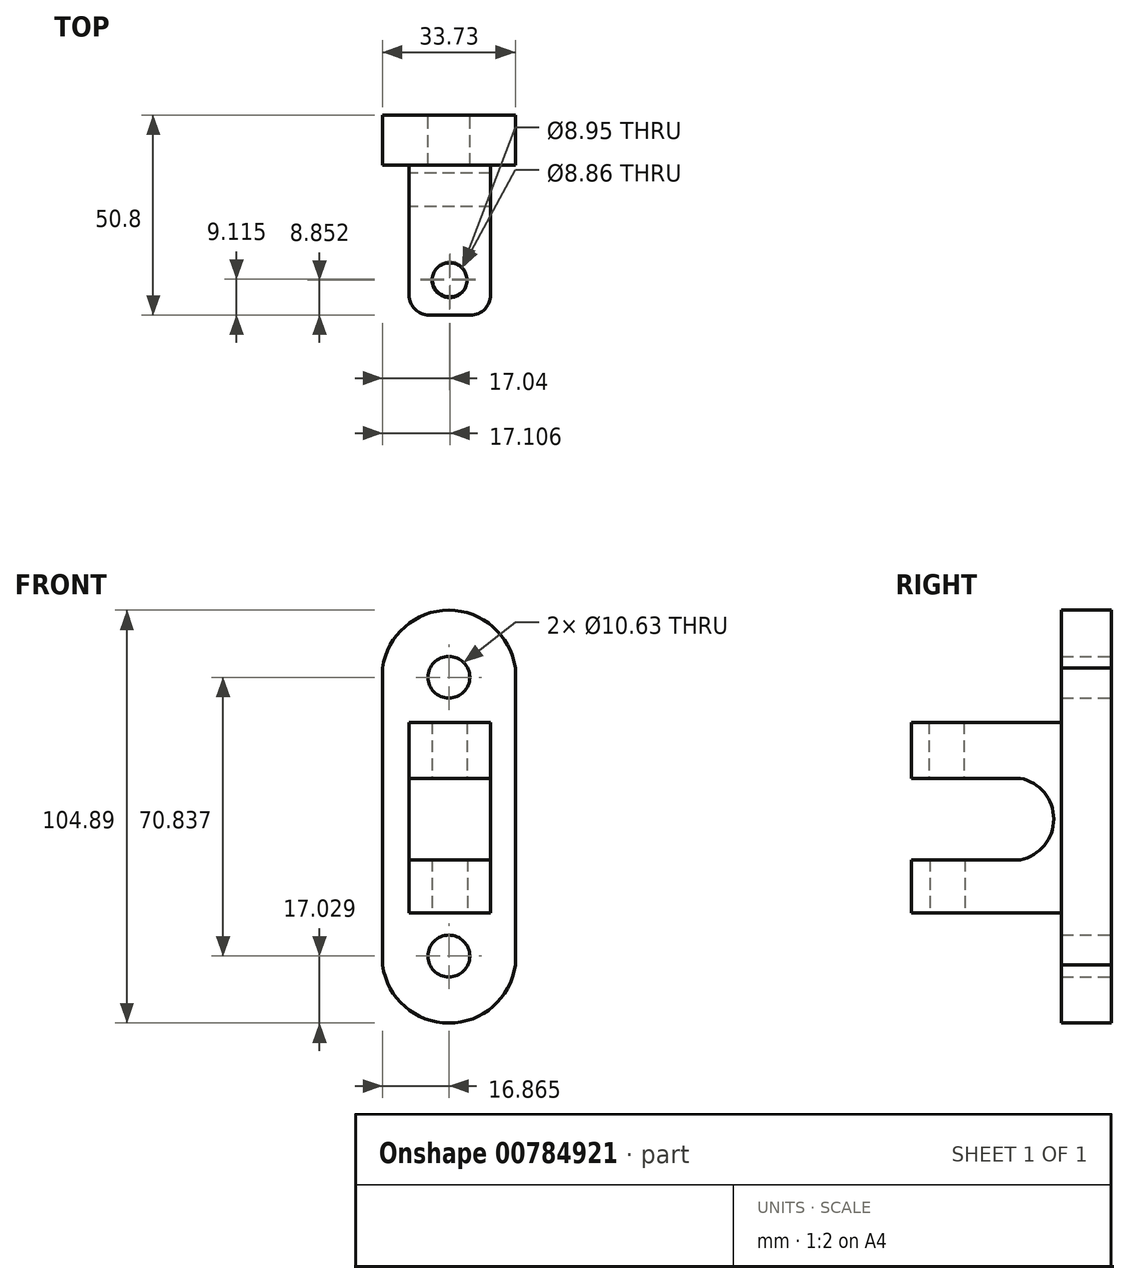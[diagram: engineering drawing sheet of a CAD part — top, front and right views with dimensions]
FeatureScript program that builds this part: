
annotation { "Feature Type Name" : "Feature", "Feature Type Description" : "" }
export const myFeature = defineFeature(function(context is Context, id is Id, definition is map)
    precondition{}
    {
        {
            var Q0;
            Q0=qCreatedBy(makeId("Front.planeOp"),FACE);
            var sketch = newSketch(context, id + "F0", { "sketchPlane" : qUnion([Q0])});
            skLineSegment(sketch, "E0", {"start": v(-23.01, 39.4) * mm, "end": v(-23.01, -36.03) * mm});
            skLineSegment(sketch, "E1", {"start": v(10.72, 39.4) * mm, "end": v(10.72, -36.03) * mm});
            skArc(sketch, "E2", {"start": v(10.72, 39.4) * mm, "mid": v(-6.15, 54.13) * mm, "end": v(-23.01, 39.4) * mm});
            skArc(sketch, "E3", {"start": v(-23.01, -36.03) * mm, "mid": v(-6.15, -50.76) * mm, "end": v(10.72, -36.03) * mm});
            skCircle(sketch, "E4", {"center": v(-6.15, 37.1) * mm, "radius": 5.31 * mm});
            skCircle(sketch, "E5", {"center": v(-6.15, -33.73) * mm, "radius": 5.31 * mm});
            skSolve(sketch);
        }
        {
            var Q0;
            Q0 = qSketchRegion(id + "F0", true);
            extrude(context, id + "F1", {"entities" : qUnion([Q0]), "depth" : 12.7 * mm, "offsetDistance" : 25.4 * mm});
        }
        {
            var Q0;
            Q0=qCreatedBy(makeId("Front.planeOp"),FACE);
            var sketch = newSketch(context, id + "F2", { "sketchPlane" : qUnion([Q0])});
            skLineSegment(sketch, "E6.bottom", {"start": v(4.46, 25.67) * mm, "end": v(-16.27, 25.67) * mm});
            skLineSegment(sketch, "E6.top", {"start": v(4.46, 11.45) * mm, "end": v(-16.27, 11.45) * mm});
            skLineSegment(sketch, "E6.left", {"start": v(4.46, 25.67) * mm, "end": v(4.46, 11.45) * mm});
            skLineSegment(sketch, "E6.right", {"start": v(-16.27, 25.67) * mm, "end": v(-16.27, 11.45) * mm});
            skLineSegment(sketch, "E7.bottom", {"start": v(4.46, -9.28) * mm, "end": v(-16.27, -9.28) * mm});
            skLineSegment(sketch, "E7.top", {"start": v(4.46, -22.77) * mm, "end": v(-16.27, -22.77) * mm});
            skLineSegment(sketch, "E7.left", {"start": v(4.46, -9.28) * mm, "end": v(4.46, -22.77) * mm});
            skLineSegment(sketch, "E7.right", {"start": v(-16.27, -9.28) * mm, "end": v(-16.27, -22.77) * mm});
            skSolve(sketch);
        }
        {
            var Q0;
            Q0 = qSketchRegion(id + "F2", true);
            extrude(context, id + "F3", {"entities" : qUnion([Q0]), "operationType" : NewBodyOperationType.ADD, "depth" : 50.8 * mm, "offsetDistance" : 25.4 * mm});
        }
        {
            var Q0;
            Q0=makeQuery(id+"F3.opExtrude","CAP_EDGE",EDGE,{"disambiguationData":[OSD([sQuery(id+"F2.wireOp",EDGE,"E6.left")])],"isStart":false});
            var Q1;
            Q1=makeQuery(id+"F3.opExtrude","CAP_EDGE",EDGE,{"disambiguationData":[OSD([sQuery(id+"F2.wireOp",EDGE,"E6.right")])],"isStart":false});
            var Q2;
            Q2=makeQuery(id+"F3.opExtrude","CAP_EDGE",EDGE,{"disambiguationData":[OSD([sQuery(id+"F2.wireOp",EDGE,"E7.left")])],"isStart":false});
            var Q3;
            Q3=makeQuery(id+"F3.opExtrude","CAP_EDGE",EDGE,{"disambiguationData":[OSD([sQuery(id+"F2.wireOp",EDGE,"E7.right")])],"isStart":false});
            fillet(context, id + "F4", {"entities" : qUnion([Q0, Q1, Q2, Q3]), "radius" : 5.08 * mm, "tangentPropagation" : true, "allowEdgeOverflow" : false});
        }
        {
            var Q0;
            Q0=makeQuery(id+"F3.opExtrude","SWEPT_FACE",FACE,{"disambiguationData":[OSD([sQuery(id+"F2.wireOp",EDGE,"E7.top")])]});
            var sketch = newSketch(context, id + "F5", { "sketchPlane" : qUnion([Q0])});
            skCircle(sketch, "E8", {"center": v(-5.9, 41.68) * mm, "radius": 4.47 * mm});
            skPoint(sketch, "E8.centerSnap0", {"position": v(-5.9, 50.8) * mm});
            skSolve(sketch);
        }
        {
            var Q0;
            Q0=makeQuery(id+"F5.imprint","IMPRINT",FACE,{"disambiguationData":[TD([[makeQuery(id+"F5.imprint","IMPRINT",EDGE,{"derivedFrom":sQuery(id+"F5.wireOp",EDGE,"E8")}),1.0]])]});
            var Q1;
            Q1=sQuery(id+"F5.wireOp",EDGE,"E8");
            extrude(context, id + "F6", {"entities" : qUnion([Q0]), "operationType" : NewBodyOperationType.REMOVE, "surfaceEntities" : qUnion([Q1]), "oppositeDirection" : true, "depth" : 25.4 * mm, "offsetDistance" : 25.4 * mm});
        }
        {
            var Q0;
            Q0=makeQuery(id+"F3.opExtrude","SWEPT_FACE",FACE,{"disambiguationData":[OSD([sQuery(id+"F2.wireOp",EDGE,"E6.top")])]});
            var sketch = newSketch(context, id + "F7", { "sketchPlane" : qUnion([Q0])});
            skCircle(sketch, "E9", {"center": v(-5.97, 41.95) * mm, "radius": 4.43 * mm});
            skSolve(sketch);
        }
        {
            var Q0;
            Q0=makeQuery(id+"F7.imprint","IMPRINT",FACE,{"disambiguationData":[TD([[makeQuery(id+"F7.imprint","IMPRINT",EDGE,{"derivedFrom":sQuery(id+"F7.wireOp",EDGE,"E9")}),1.0]])]});
            extrude(context, id + "F8", {"entities" : qUnion([Q0]), "operationType" : NewBodyOperationType.REMOVE, "oppositeDirection" : true, "depth" : 25.4 * mm, "offsetDistance" : 25.4 * mm});
        }
        {
            var Q0;
            Q0=makeQuery(id+"F3.opExtrude","SWEPT_FACE",FACE,{"disambiguationData":[OSD([sQuery(id+"F2.wireOp",EDGE,"E7.bottom")])]});
            var sketch = newSketch(context, id + "F9", { "sketchPlane" : qUnion([Q0])});
            skLineSegment(sketch, "E10", {"start": v(4.46, -23.22) * mm, "end": v(-16.27, -23.22) * mm});
            skSolve(sketch);
        }
        {
            var Q0;
            {var subQ0=sQuery(id+"F9.wireOp",EDGE,"E10");Q0=makeQuery(id+"F9.imprint","IMPRINT",FACE,{"disambiguationData":[TD([[makeQuery(id+"F9.imprint","IMPRINT",EDGE,{"derivedFrom":subQ0}),-1.0]])]});}
            extrude(context, id + "F10", {"entities" : qUnion([Q0]), "operationType" : NewBodyOperationType.ADD, "depth" : 25.4 * mm, "offsetDistance" : 25.4 * mm});
        }
        {
            var Q0;
            {var subQ0=sQuery(id+"F2.wireOp",EDGE,"E7.right");Q0=makeQuery(id+"F10.boolean.opBoolean","MERGE",FACE,{"derivedFrom":[makeQuery(id+"F3.opExtrude","SWEPT_FACE",FACE,{"disambiguationData":[OSD([sQuery(id+"F2.wireOp",EDGE,"E6.right")])]}),makeQuery(id+"F3.opExtrude","SWEPT_FACE",FACE,{"disambiguationData":[OSD([subQ0])]}),makeQuery(id+"F10.opExtrude","SWEPT_FACE",FACE,{"disambiguationData":[OSD([sQuery(id+"F2.wireOp",EDGE,"E7.bottom"),subQ0])]})]});}
            var sketch = newSketch(context, id + "F11", { "sketchPlane" : qUnion([Q0])});
            skArc(sketch, "E11", {"start": v(23.22, 11.45) * mm, "mid": v(14.69, 1.08) * mm, "end": v(23.22, -9.28) * mm});
            skSolve(sketch);
        }
        {
            var Q0;
            Q0=makeQuery(id+"F11.imprint","IMPRINT",FACE,{"disambiguationData":[TD([[makeQuery(id+"F11.imprint","IMPRINT",EDGE,{"derivedFrom":sQuery(id+"F11.wireOp",EDGE,"E11")}),1.0]])]});
            extrude(context, id + "F12", {"entities" : qUnion([Q0]), "operationType" : NewBodyOperationType.REMOVE, "oppositeDirection" : true, "depth" : 25.4 * mm, "offsetDistance" : 25.4 * mm});
        }
    });
